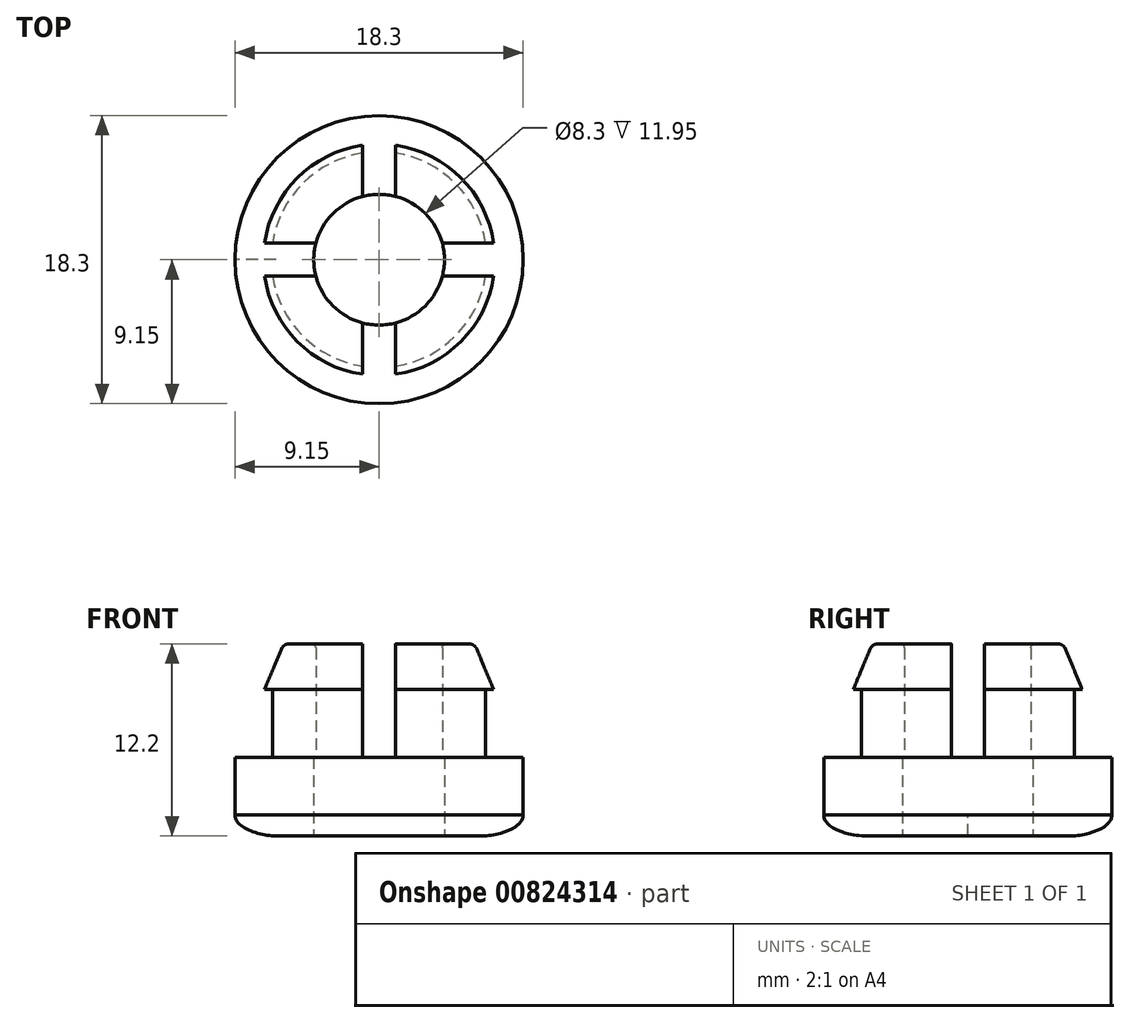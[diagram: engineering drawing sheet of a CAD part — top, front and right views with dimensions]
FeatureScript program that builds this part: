
annotation { "Feature Type Name" : "Feature", "Feature Type Description" : "" }
export const myFeature = defineFeature(function(context is Context, id is Id, definition is map)
    precondition{}
    {
        {
            var Q0;
            Q0=qCreatedBy(makeId("Front.planeOp"),FACE);
            var sketch = newSketch(context, id + "F0", { "sketchPlane" : qUnion([Q0])});
            skLineSegment(sketch, "E0", {"start": v(0, 0) * mm, "end": v(0, 9.13) * mm, "construction": true});
            skLineSegment(sketch, "E1", {"start": v(0, 0) * mm, "end": v(4.15, 0) * mm, "construction": true});
            skLineSegment(sketch, "E2", {"start": v(4.15, 0) * mm, "end": v(6.55, 0) * mm});
            skFitSpline(sketch, "E3", {"points": [v(6.55, 0) * mm, v(9.15, 1.34) * mm], "startDerivative": vector(2.9, 0) * mm, "endDerivative": vector(0, 2.67) * mm});
            skLineSegment(sketch, "E4", {"start": v(9.15, 1.34) * mm, "end": v(9.15, 5) * mm});
            skLineSegment(sketch, "E5", {"start": v(9.15, 5) * mm, "end": v(6.85, 5) * mm});
            skLineSegment(sketch, "E6", {"start": v(6.85, 5) * mm, "end": v(6.85, 9.3) * mm});
            skLineSegment(sketch, "E7", {"start": v(6.85, 9.3) * mm, "end": v(7.35, 9.3) * mm});
            skLineSegment(sketch, "E8", {"start": v(6.15, 12.2) * mm, "end": v(4.15, 12.2) * mm});
            skLineSegment(sketch, "E9", {"start": v(4.15, 12.2) * mm, "end": v(4.15, 0) * mm});
            skLineSegment(sketch, "E10", {"start": v(6.15, 12.2) * mm, "end": v(7.35, 9.3) * mm});
            skSolve(sketch);
        }
        {
            var Q0;
            Q0=makeQuery(id+"F0.imprint","IMPRINT",FACE,{"disambiguationData":[TD([[makeQuery(id+"F0.imprint","IMPRINT",EDGE,{"derivedFrom":sQuery(id+"F0.wireOp",EDGE,"E2")}),1.0]])]});
            var Q1;
            Q1=sQuery(id+"F0.wireOp",EDGE,"E0");
            revolve(context, id + "F1", {"surfaceOperationType" : NewSurfaceOperationType.NEW, "entities" : qUnion([Q0]), "axis" : qUnion([Q1]), "revolveType" : RevolveType.FULL});
        }
        {
            var Q0;
            Q0=makeQuery(id+"F1.opRevolve","SWEPT_FACE",FACE,{"disambiguationData":[OSD([sQuery(id+"F0.wireOp",EDGE,"E8")])]});
            var sketch = newSketch(context, id + "F2", { "sketchPlane" : qUnion([Q0])});
            skLineSegment(sketch, "E11", {"start": v(1.05, 7.5) * mm, "end": v(1.05, -7.5) * mm});
            skLineSegment(sketch, "E12.MirrorCS", {"start": v(-1.05, 7.5) * mm, "end": v(-1.05, -7.5) * mm});
            skLineSegment(sketch, "E13", {"start": v(-1.05, 7.5) * mm, "end": v(1.05, 7.5) * mm});
            skLineSegment(sketch, "E14", {"start": v(-1.05, -7.5) * mm, "end": v(1.05, -7.5) * mm});
            skLineSegment(sketch, "E15", {"start": v(-7.5, 1.05) * mm, "end": v(7.5, 1.05) * mm});
            skLineSegment(sketch, "E16", {"start": v(7.5, 1.05) * mm, "end": v(7.5, -1.05) * mm});
            skLineSegment(sketch, "E17", {"start": v(7.5, -1.05) * mm, "end": v(-7.5, -1.05) * mm});
            skLineSegment(sketch, "E18", {"start": v(-7.5, -1.05) * mm, "end": v(-7.5, 1.05) * mm});
            skSolve(sketch);
        }
        {
            var Q0;
            Q0 = qSketchRegion(id + "F2", true);
            extrude(context, id + "F3", {"entities" : qUnion([Q0]), "operationType" : NewBodyOperationType.REMOVE, "oppositeDirection" : true, "depth" : 7.2 * mm, "offsetDistance" : 25 * mm});
        }
        {
            var Q0;
            {var subQ0=sQuery(id+"F0.wireOp",EDGE,"E8");var subQ1=sQuery(id+"F0.wireOp",EDGE,"E9");var subQ2=sQuery(id+"F2.wireOp",EDGE,"E12.MirrorCS");var subQ3=makeQuery(id+"F1.opRevolve","SWEPT_EDGE",EDGE,{"disambiguationData":[OSD([subQ0,sQuery(id+"F0.wireOp",EDGE,"E10")])]});var subQ4=makeQuery(id+"F2.imprint","INTERSECT",VERTEX,{"disambiguationData":[OD(1.0)],"derivedFrom":[subQ3,subQ2]});var subQ5=makeQuery(id+"F1.opRevolve","SWEPT_EDGE",EDGE,{"disambiguationData":[OSD([subQ0,subQ1])]});var subQ7=sQuery(id+"F2.wireOp",EDGE,"E17");var subQ8=makeQuery(id+"F2.imprint","INTERSECT",VERTEX,{"derivedFrom":[subQ2,subQ7]});Q0=makeQuery(id+"F3.boolean.opBoolean","SPLIT",EDGE,{"disambiguationData":[TD([makeQuery(id+"F3.opExtrude","SWEPT_FACE",FACE,{"disambiguationData":[OSD([subQ2]),TDD([makeQuery(id+"F2.imprint","IMPRINT",EDGE,{"disambiguationData":[TD([[subQ8,-1.0]])],"derivedFrom":subQ2}),makeQuery(id+"F2.imprint","IMPRINT",EDGE,{"disambiguationData":[TD([[subQ4,1.0]])],"derivedFrom":subQ2}),makeQuery(id+"F2.imprint","IMPRINT",EDGE,{"disambiguationData":[TD([[makeQuery(id+"F2.imprint","INTERSECT",VERTEX,{"derivedFrom":[subQ2,sQuery(id+"F2.wireOp",EDGE,"E14")]}),1.0]])],"derivedFrom":subQ2})])]})])],"derivedFrom":subQ5});}
            var Q1;
            {var subQ0=sQuery(id+"F0.wireOp",EDGE,"E8");var subQ1=sQuery(id+"F2.wireOp",EDGE,"E15");var subQ2=sQuery(id+"F2.wireOp",EDGE,"E12.MirrorCS");var subQ3=makeQuery(id+"F2.imprint","INTERSECT",VERTEX,{"derivedFrom":[subQ2,subQ1]});var subQ4=sQuery(id+"F0.wireOp",EDGE,"E9");var subQ5=makeQuery(id+"F1.opRevolve","SWEPT_EDGE",EDGE,{"disambiguationData":[OSD([subQ0,subQ4])]});var subQ7=makeQuery(id+"F1.opRevolve","SWEPT_EDGE",EDGE,{"disambiguationData":[OSD([subQ0,sQuery(id+"F0.wireOp",EDGE,"E10")])]});var subQ10=makeQuery(id+"F2.imprint","INTERSECT",VERTEX,{"disambiguationData":[OD(0.0)],"derivedFrom":[subQ7,subQ2]});Q1=makeQuery(id+"F3.boolean.opBoolean","SPLIT",EDGE,{"disambiguationData":[TD([makeQuery(id+"F3.opExtrude","SWEPT_FACE",FACE,{"disambiguationData":[OSD([subQ2]),TDD([makeQuery(id+"F2.imprint","IMPRINT",EDGE,{"disambiguationData":[TD([[makeQuery(id+"F2.imprint","INTERSECT",VERTEX,{"derivedFrom":[subQ2,sQuery(id+"F2.wireOp",EDGE,"E13")]}),-1.0]])],"derivedFrom":subQ2}),makeQuery(id+"F2.imprint","IMPRINT",EDGE,{"disambiguationData":[TD([[subQ10,-1.0]])],"derivedFrom":subQ2}),makeQuery(id+"F2.imprint","IMPRINT",EDGE,{"disambiguationData":[TD([[subQ3,1.0]])],"derivedFrom":subQ2})])]})])],"derivedFrom":subQ5});}
            var Q2;
            {var subQ0=sQuery(id+"F0.wireOp",EDGE,"E8");var subQ1=sQuery(id+"F0.wireOp",EDGE,"E9");var subQ2=sQuery(id+"F2.wireOp",EDGE,"E15");var subQ3=makeQuery(id+"F1.opRevolve","SWEPT_EDGE",EDGE,{"disambiguationData":[OSD([subQ0,sQuery(id+"F0.wireOp",EDGE,"E10")])]});var subQ5=makeQuery(id+"F1.opRevolve","SWEPT_EDGE",EDGE,{"disambiguationData":[OSD([subQ0,subQ1])]});var subQ7=sQuery(id+"F2.wireOp",EDGE,"E11");var subQ8=makeQuery(id+"F2.imprint","INTERSECT",VERTEX,{"derivedFrom":[subQ7,subQ2]});var subQ10=makeQuery(id+"F2.imprint","INTERSECT",VERTEX,{"disambiguationData":[OD(0.0)],"derivedFrom":[subQ3,subQ7]});Q2=makeQuery(id+"F3.boolean.opBoolean","SPLIT",EDGE,{"disambiguationData":[TD([makeQuery(id+"F3.opExtrude","SWEPT_FACE",FACE,{"disambiguationData":[OSD([subQ7]),TDD([makeQuery(id+"F2.imprint","IMPRINT",EDGE,{"disambiguationData":[TD([[makeQuery(id+"F2.imprint","INTERSECT",VERTEX,{"derivedFrom":[subQ7,sQuery(id+"F2.wireOp",EDGE,"E13")]}),-1.0]])],"derivedFrom":subQ7}),makeQuery(id+"F2.imprint","IMPRINT",EDGE,{"disambiguationData":[TD([[subQ10,-1.0]])],"derivedFrom":subQ7}),makeQuery(id+"F2.imprint","IMPRINT",EDGE,{"disambiguationData":[TD([[subQ8,1.0]])],"derivedFrom":subQ7})])]})])],"derivedFrom":subQ5});}
            var Q3;
            {var subQ0=sQuery(id+"F0.wireOp",EDGE,"E8");var subQ1=sQuery(id+"F2.wireOp",EDGE,"E11");var subQ2=makeQuery(id+"F1.opRevolve","SWEPT_EDGE",EDGE,{"disambiguationData":[OSD([subQ0,sQuery(id+"F0.wireOp",EDGE,"E10")])]});var subQ3=makeQuery(id+"F2.imprint","INTERSECT",VERTEX,{"disambiguationData":[OD(1.0)],"derivedFrom":[subQ2,subQ1]});var subQ4=sQuery(id+"F0.wireOp",EDGE,"E9");var subQ5=makeQuery(id+"F1.opRevolve","SWEPT_EDGE",EDGE,{"disambiguationData":[OSD([subQ0,subQ4])]});var subQ7=sQuery(id+"F2.wireOp",EDGE,"E17");var subQ8=makeQuery(id+"F2.imprint","INTERSECT",VERTEX,{"derivedFrom":[subQ1,subQ7]});Q3=makeQuery(id+"F3.boolean.opBoolean","SPLIT",EDGE,{"disambiguationData":[TD([makeQuery(id+"F3.opExtrude","SWEPT_FACE",FACE,{"disambiguationData":[OSD([subQ1]),TDD([makeQuery(id+"F2.imprint","IMPRINT",EDGE,{"disambiguationData":[TD([[subQ8,-1.0]])],"derivedFrom":subQ1}),makeQuery(id+"F2.imprint","IMPRINT",EDGE,{"disambiguationData":[TD([[subQ3,1.0]])],"derivedFrom":subQ1}),makeQuery(id+"F2.imprint","IMPRINT",EDGE,{"disambiguationData":[TD([[makeQuery(id+"F2.imprint","INTERSECT",VERTEX,{"derivedFrom":[subQ1,sQuery(id+"F2.wireOp",EDGE,"E14")]}),1.0]])],"derivedFrom":subQ1})])]})])],"derivedFrom":subQ5});}
            fillet(context, id + "F4", {"entities" : qUnion([Q0, Q1, Q2, Q3]), "radius" : 0.25 * mm, "tangentPropagation" : true, "allowEdgeOverflow" : false});
        }
        {
            var Q0;
            {var subQ0=sQuery(id+"F0.wireOp",EDGE,"E8");var subQ1=sQuery(id+"F0.wireOp",EDGE,"E10");var subQ2=sQuery(id+"F2.wireOp",EDGE,"E15");var subQ3=sQuery(id+"F2.wireOp",EDGE,"E11");var subQ4=makeQuery(id+"F2.imprint","INTERSECT",VERTEX,{"derivedFrom":[subQ3,subQ2]});var subQ7=makeQuery(id+"F1.opRevolve","SWEPT_EDGE",EDGE,{"disambiguationData":[OSD([subQ0,subQ1])]});var subQ8=makeQuery(id+"F2.imprint","INTERSECT",VERTEX,{"disambiguationData":[OD(0.0)],"derivedFrom":[subQ7,subQ3]});Q0=makeQuery(id+"F3.boolean.opBoolean","SPLIT",EDGE,{"disambiguationData":[TD([makeQuery(id+"F3.opExtrude","SWEPT_FACE",FACE,{"disambiguationData":[OSD([subQ3]),TDD([makeQuery(id+"F2.imprint","IMPRINT",EDGE,{"disambiguationData":[TD([[makeQuery(id+"F2.imprint","INTERSECT",VERTEX,{"derivedFrom":[subQ3,sQuery(id+"F2.wireOp",EDGE,"E13")]}),-1.0]])],"derivedFrom":subQ3}),makeQuery(id+"F2.imprint","IMPRINT",EDGE,{"disambiguationData":[TD([[subQ8,-1.0]])],"derivedFrom":subQ3}),makeQuery(id+"F2.imprint","IMPRINT",EDGE,{"disambiguationData":[TD([[subQ4,1.0]])],"derivedFrom":subQ3})])]})])],"derivedFrom":subQ7});}
            var Q1;
            {var subQ0=sQuery(id+"F0.wireOp",EDGE,"E8");var subQ1=sQuery(id+"F2.wireOp",EDGE,"E15");var subQ2=sQuery(id+"F2.wireOp",EDGE,"E12.MirrorCS");var subQ3=makeQuery(id+"F2.imprint","INTERSECT",VERTEX,{"derivedFrom":[subQ2,subQ1]});var subQ6=sQuery(id+"F0.wireOp",EDGE,"E10");var subQ7=makeQuery(id+"F1.opRevolve","SWEPT_EDGE",EDGE,{"disambiguationData":[OSD([subQ0,subQ6])]});var subQ10=makeQuery(id+"F2.imprint","INTERSECT",VERTEX,{"disambiguationData":[OD(0.0)],"derivedFrom":[subQ7,subQ2]});Q1=makeQuery(id+"F3.boolean.opBoolean","SPLIT",EDGE,{"disambiguationData":[TD([makeQuery(id+"F3.opExtrude","SWEPT_FACE",FACE,{"disambiguationData":[OSD([subQ2]),TDD([makeQuery(id+"F2.imprint","IMPRINT",EDGE,{"disambiguationData":[TD([[makeQuery(id+"F2.imprint","INTERSECT",VERTEX,{"derivedFrom":[subQ2,sQuery(id+"F2.wireOp",EDGE,"E13")]}),-1.0]])],"derivedFrom":subQ2}),makeQuery(id+"F2.imprint","IMPRINT",EDGE,{"disambiguationData":[TD([[subQ10,-1.0]])],"derivedFrom":subQ2}),makeQuery(id+"F2.imprint","IMPRINT",EDGE,{"disambiguationData":[TD([[subQ3,1.0]])],"derivedFrom":subQ2})])]})])],"derivedFrom":subQ7});}
            var Q2;
            {var subQ0=sQuery(id+"F0.wireOp",EDGE,"E8");var subQ1=sQuery(id+"F0.wireOp",EDGE,"E10");var subQ2=sQuery(id+"F2.wireOp",EDGE,"E12.MirrorCS");var subQ3=makeQuery(id+"F1.opRevolve","SWEPT_EDGE",EDGE,{"disambiguationData":[OSD([subQ0,subQ1])]});var subQ4=makeQuery(id+"F2.imprint","INTERSECT",VERTEX,{"disambiguationData":[OD(1.0)],"derivedFrom":[subQ3,subQ2]});var subQ7=sQuery(id+"F2.wireOp",EDGE,"E17");var subQ8=makeQuery(id+"F2.imprint","INTERSECT",VERTEX,{"derivedFrom":[subQ2,subQ7]});Q2=makeQuery(id+"F3.boolean.opBoolean","SPLIT",EDGE,{"disambiguationData":[TD([makeQuery(id+"F3.opExtrude","SWEPT_FACE",FACE,{"disambiguationData":[OSD([subQ2]),TDD([makeQuery(id+"F2.imprint","IMPRINT",EDGE,{"disambiguationData":[TD([[subQ8,-1.0]])],"derivedFrom":subQ2}),makeQuery(id+"F2.imprint","IMPRINT",EDGE,{"disambiguationData":[TD([[subQ4,1.0]])],"derivedFrom":subQ2}),makeQuery(id+"F2.imprint","IMPRINT",EDGE,{"disambiguationData":[TD([[makeQuery(id+"F2.imprint","INTERSECT",VERTEX,{"derivedFrom":[subQ2,sQuery(id+"F2.wireOp",EDGE,"E14")]}),1.0]])],"derivedFrom":subQ2})])]})])],"derivedFrom":subQ3});}
            var Q3;
            {var subQ0=sQuery(id+"F0.wireOp",EDGE,"E8");var subQ1=sQuery(id+"F2.wireOp",EDGE,"E11");var subQ2=sQuery(id+"F0.wireOp",EDGE,"E10");var subQ3=makeQuery(id+"F1.opRevolve","SWEPT_EDGE",EDGE,{"disambiguationData":[OSD([subQ0,subQ2])]});var subQ4=makeQuery(id+"F2.imprint","INTERSECT",VERTEX,{"disambiguationData":[OD(1.0)],"derivedFrom":[subQ3,subQ1]});var subQ7=sQuery(id+"F2.wireOp",EDGE,"E17");var subQ8=makeQuery(id+"F2.imprint","INTERSECT",VERTEX,{"derivedFrom":[subQ1,subQ7]});Q3=makeQuery(id+"F3.boolean.opBoolean","SPLIT",EDGE,{"disambiguationData":[TD([makeQuery(id+"F3.opExtrude","SWEPT_FACE",FACE,{"disambiguationData":[OSD([subQ1]),TDD([makeQuery(id+"F2.imprint","IMPRINT",EDGE,{"disambiguationData":[TD([[subQ8,-1.0]])],"derivedFrom":subQ1}),makeQuery(id+"F2.imprint","IMPRINT",EDGE,{"disambiguationData":[TD([[subQ4,1.0]])],"derivedFrom":subQ1}),makeQuery(id+"F2.imprint","IMPRINT",EDGE,{"disambiguationData":[TD([[makeQuery(id+"F2.imprint","INTERSECT",VERTEX,{"derivedFrom":[subQ1,sQuery(id+"F2.wireOp",EDGE,"E14")]}),1.0]])],"derivedFrom":subQ1})])]})])],"derivedFrom":subQ3});}
            fillet(context, id + "F5", {"entities" : qUnion([Q0, Q1, Q2, Q3]), "radius" : 0.5 * mm, "tangentPropagation" : true, "allowEdgeOverflow" : false});
        }
    });
